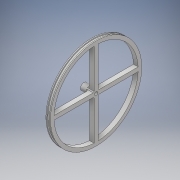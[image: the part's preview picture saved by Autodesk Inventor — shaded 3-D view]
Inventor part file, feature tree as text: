
AUTODESK INVENTOR PART (.ipt)
format: ipt  version: 2018 (Build 220112000, 112)  size: 378,880 bytes
history: native  units: mm
features: extrude x12, sketch x12, pattern_circular x1, fillet x1
ambient origin geometry x8: Origin, YZ Plane, XZ Plane, XY Plane, X Axis, Y Axis, Z Axis, Center Point
bodies: Solid1 (feature_tree)
feature tree (26):
  extrude  "Extrusion1"  Depth=3.5mm TaperAngle=0.0deg
  extrude  "Extrusion2"  Depth=1.0mm TaperAngle=0.0deg
  extrude  "Extrusion3"  Depth=1.0mm TaperAngle=0.0deg
  extrude  "Extrusion4"  Depth=6.0mm TaperAngle=0.0deg
  extrude  "Extrusion5"  Depth=10.0mm TaperAngle=0.0deg
  extrude  "Extrusion6"  Depth=1.0mm TaperAngle=0.0deg
  extrude  "Extrusion7"  Depth=1.0mm
  extrude  "Extrusion8"  Depth=4.0mm
  extrude  "Extrusion9"  Depth=40.0mm TaperAngle=360.0deg
  extrude  "Extrusion10"  Depth=2.0mm TaperAngle=0.0deg
  pattern_circular  "Circular Pattern1"  [2 undecoded]
  fillet  "Fillet1"  [1 undecoded]
  extrude  "Extrusion11"  [1 undecoded]
  extrude  "Extrusion12"  [1 undecoded]
  sketch  "Sketch1"  dims[d0=88.0mm d1=3.5mm d2=0.0mm]
  sketch  "Sketch2"  dims[d3=90.0mm d4=1.0mm d5=0.0mm]
  sketch  "Sketch3"  dims[d6=90.0mm d7=1.0mm d8=0.0mm]
  sketch  "Sketch4"  dims[d9=83.0mm d10=6.0mm d11=0.0mm]
  sketch  "Sketch5"  dims[d12=7.0mm d13=10.0mm d14=0.0mm]
  sketch  "Sketch6"  dims[d15=2.0mm d16=0.0mm d17=1.0mm d18=0.0mm]
  sketch  "Sketch7"  dims[d19=1.0mm d20=0.0mm d21=3.25mm]
  sketch  "Sketch8"  dims[d22=10.0mm d23=0.0mm d24=4.0mm]
  sketch  "Sketch9"  dims[d25=4.5mm d26=0.0mm d27=40.0mm d28=360.0deg]
  sketch  "Sketch10"  dims[d30=2.0mm d31=2.0mm d32=0.0mm]
  sketch  "Sketch11"  dims[d33=1.0mm d34=0.0mm]
  sketch  "Sketch12"
note: 5 required parameter values undecoded (feature->parameter linkage not recoverable at this tier; creation-order binding heuristic only, values carry confidence <= 0.55)
